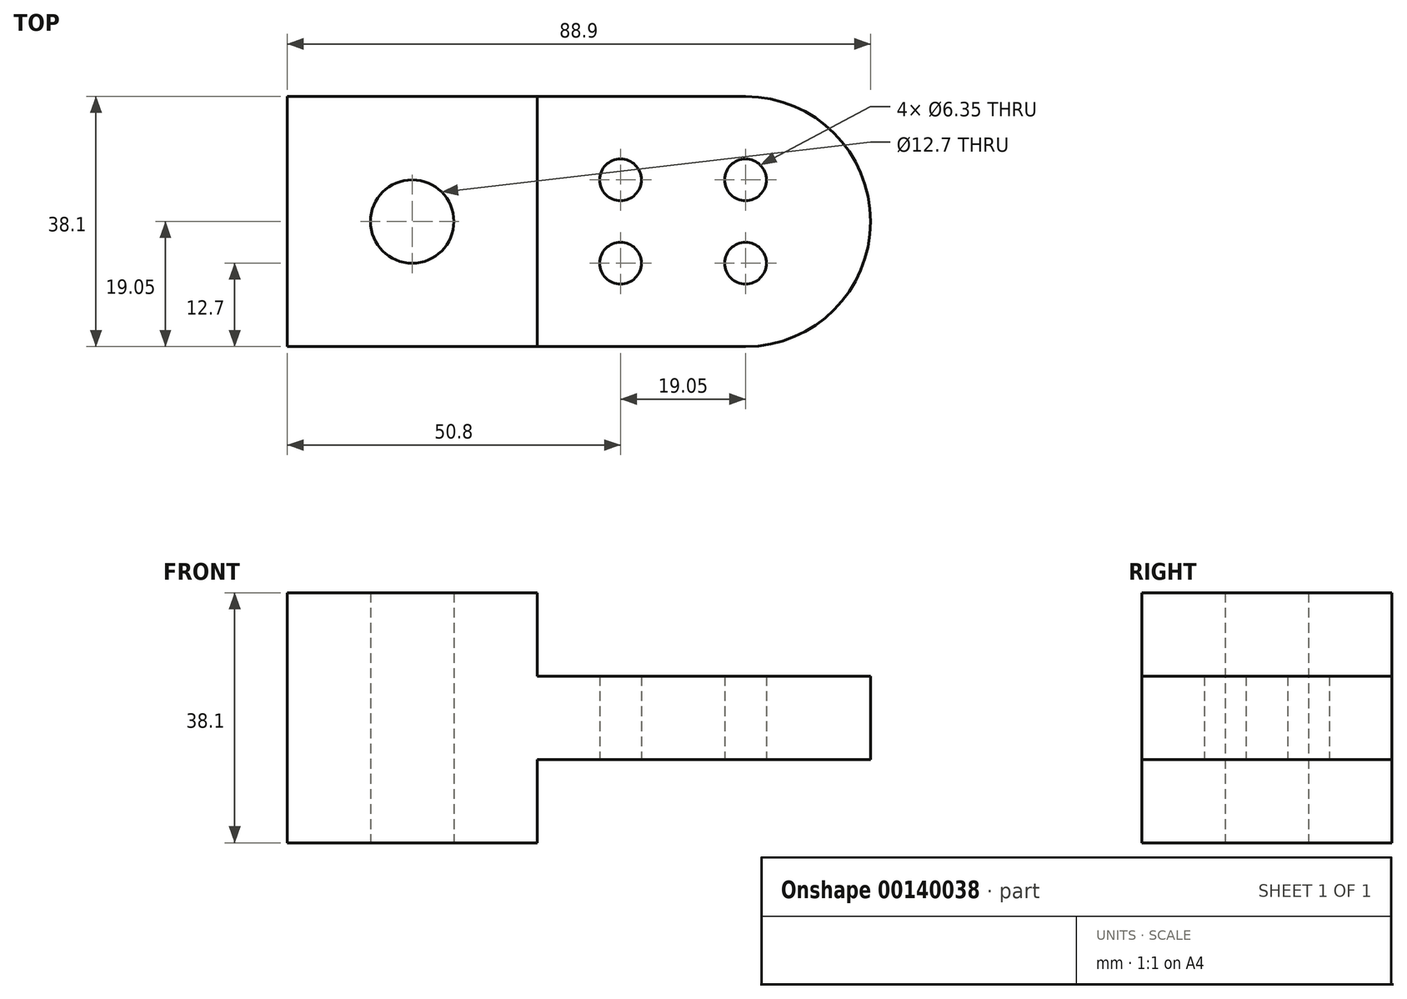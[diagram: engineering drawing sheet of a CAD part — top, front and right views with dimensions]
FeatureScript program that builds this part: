
annotation { "Feature Type Name" : "Feature", "Feature Type Description" : "" }
export const myFeature = defineFeature(function(context is Context, id is Id, definition is map)
    precondition{}
    {
        {
            var Q0;
            Q0=qCreatedBy(makeId("Top.planeOp"),FACE);
            var sketch = newSketch(context, id + "F0", { "sketchPlane" : qUnion([Q0])});
            skLineSegment(sketch, "E0", {"start": v(0, 38.1) * mm, "end": v(0, 0) * mm});
            skLineSegment(sketch, "E1", {"start": v(0, 0) * mm, "end": v(38.1, 0) * mm});
            skLineSegment(sketch, "E2", {"start": v(38.1, 0) * mm, "end": v(38.1, 38.1) * mm});
            skLineSegment(sketch, "E3", {"start": v(38.1, 38.1) * mm, "end": v(0, 38.1) * mm});
            skLineSegment(sketch, "E4", {"start": v(38.1, 38.1) * mm, "end": v(69.85, 38.1) * mm});
            skLineSegment(sketch, "E5", {"start": v(38.1, 0) * mm, "end": v(69.85, 0) * mm});
            skLineSegment(sketch, "E6", {"start": v(69.85, 68.7) * mm, "end": v(69.85, -47.84) * mm, "construction": true});
            skArc(sketch, "E7", {"start": v(69.85, 0) * mm, "mid": v(88.9, 19.05) * mm, "end": v(69.85, 38.1) * mm});
            skCircle(sketch, "E8", {"center": v(19.05, 19.05) * mm, "radius": 6.35 * mm});
            skCircle(sketch, "E9", {"center": v(50.8, 25.4) * mm, "radius": 3.18 * mm});
            skCircle(sketch, "E10", {"center": v(69.85, 25.4) * mm, "radius": 3.18 * mm});
            skCircle(sketch, "E11", {"center": v(69.85, 12.7) * mm, "radius": 3.18 * mm});
            skCircle(sketch, "E12", {"center": v(50.8, 12.7) * mm, "radius": 3.18 * mm});
            skSolve(sketch);
        }
        {
            var Q0;
            Q0=makeQuery(id+"F0.imprint","IMPRINT",FACE,{"disambiguationData":[TD([[makeQuery(id+"F0.imprint","IMPRINT",EDGE,{"derivedFrom":sQuery(id+"F0.wireOp",EDGE,"E0")}),1.0]])]});
            extrude(context, id + "F1", {"entities" : qUnion([Q0]), "depth" : 38.1 * mm});
        }
        {
            var Q0;
            Q0=makeQuery(id+"F0.imprint","IMPRINT",FACE,{"disambiguationData":[TD([[makeQuery(id+"F0.imprint","IMPRINT",EDGE,{"derivedFrom":sQuery(id+"F0.wireOp",EDGE,"E2")}),-1.0]])]});
            extrude(context, id + "F2", {"entities" : qUnion([Q0]), "operationType" : NewBodyOperationType.ADD, "depth" : 25.4 * mm, "hasSecondDirection" : true, "secondDirectionOppositeDirection" : false, "secondDirectionDepth" : 12.7 * mm});
        }
    });
